# Revit family: HVAC_HangingSystems_Walraven_BIS_Rail_End_Cap
name_source: partatom
category: Mechanical Equipment
revit_build: Autodesk Revit MEP 2016 (Build: 20150220_1215(x64)
units: mm (PartAtom-declared; Revit-internal decimal feet)

## family parameters
Always vertical = No
Cut with Voids When Loaded = No
OmniClass Number = 23.60.30.11.17
OmniClass Title = Pipework/Ductwork Mechanical Fasteners/Supports
Part Type = Normal
Room Calculation Point = No
Round Connector Dimension = Use Diameter
Shared = No
Work Plane-Based = Yes

## types (6) — shared parameters
Assembly Code = 50
BIMobject category = Hanging Systems
BIMobject category code = hvac-hanging-systems
BIMobject main category = HVAC
BIMobject main category code = hvac
Brand url = https://www.walraven.com
Date of publishing = 7/20/2018
Default Elevation = 1219 mm
Description = rail end cap
Design country = Netherlands
IFC Classification = Mechanical Fastener
IfcDescription = rail end cap
IfcExportAs = IfcMechanicalFastenerType
IfcExportType = USERDEFINED
Manufacturer = Walraven
Manufacturer country = Netherlands
Manufacturer name = Walraven
Material main = Polyethylene
Model = BIS Rail End Cap
OmniClass Code = 23-27 43 13
OmniClass Description = Mechanical Pipe Supports
Product Guid = bbd2fa3c-0bff-439e-94bb-7e42f8bab402
Product SKU = bis-rail-end-cap
Product data url = https://bimobject.com
Product family = Rail Systems
Product group = End Caps
Product url = https://www.walraven.com
QR code = http://bimobject.com
RSen_C_code_ETIM = EC000475
RSen_C_code_ETIM_url = https://prod.etim-international.com
RSen_C_content_modification_date = 15-01-2019
RSen_C_content_releasedate = 22-02-2018
RSen_C_intended_use = hanging systems
RSen_C_level_of_development = LOD400
RSen_C_material = polyethylene (PE)
RSen_C_material_colour = green
RSen_C_material_finish = -
Technical description = https://library.walraven.com
URL = https://www.walraven.com
Weight Net (Kg) = 0
region_index = 1
zero-valued in all types: Edition number, Nominal height, Nominal width

## per-type parameters (varying)
| type | type_index |
| WM35 (38x40mm) | 3 |
| WM2 (30x30mm) | 2 |
| WM1 (30x15mm) | 1 |
| WM0 (27x18mm) | 4 |
| WM30 (30x45mm) | 5 |
| WM15 (30x20mm) | 6 |

## geometry (parser evidence)
native form markers: Blend x2, Sweep x4
no freeform markers — native parametric forms only
